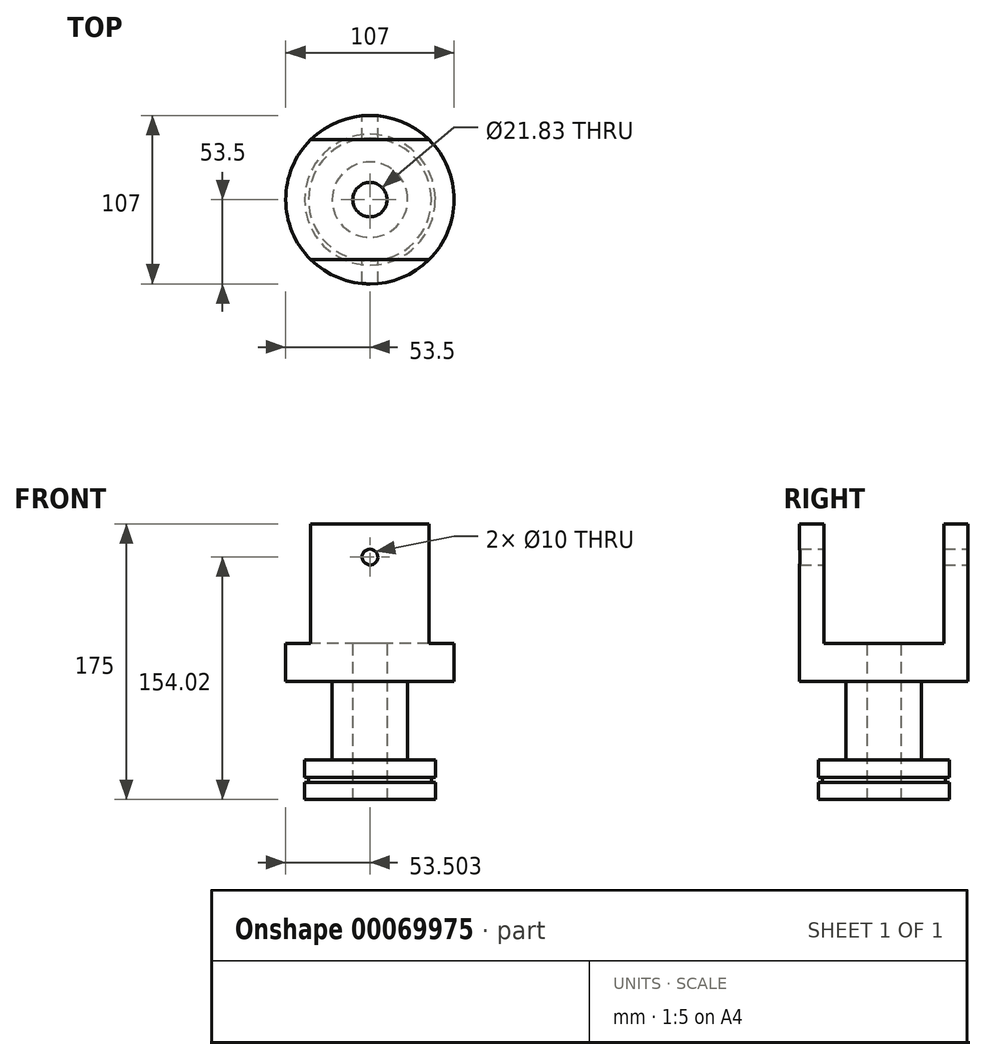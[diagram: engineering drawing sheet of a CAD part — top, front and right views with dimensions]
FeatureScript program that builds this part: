
annotation { "Feature Type Name" : "Feature", "Feature Type Description" : "" }
export const myFeature = defineFeature(function(context is Context, id is Id, definition is map)
    precondition{}
    {
        {
            var Q0;
            Q0=qCreatedBy(makeId("Top.planeOp"),FACE);
            var sketch = newSketch(context, id + "F0", { "sketchPlane" : qUnion([Q0])});
            skCircle(sketch, "E0", {"center": v(0, 0) * mm, "radius": 53.5 * mm});
            skCircle(sketch, "E1", {"center": v(0, 0) * mm, "radius": 10.91 * mm});
            skSolve(sketch);
        }
        {
            var Q0;
            Q0=makeQuery(id+"F0.imprint","IMPRINT",FACE,{"disambiguationData":[TD([[makeQuery(id+"F0.imprint","IMPRINT",EDGE,{"derivedFrom":sQuery(id+"F0.wireOp",EDGE,"E0")}),1.0]])]});
            var Q1;
            Q1=makeQuery(id+"F0.imprint","IMPRINT",FACE,{"disambiguationData":[TD([[makeQuery(id+"F0.imprint","IMPRINT",EDGE,{"derivedFrom":sQuery(id+"F0.wireOp",EDGE,"bf1bf4bc-554c-4a6b-8778-0bc88469c6b6")}),1.0]])]});
            extrude(context, id + "F1", {"entities" : qUnion([Q0, Q1]), "depth" : 100 * mm});
        }
        {
            var Q0;
            Q0=makeQuery(id+"F1.opExtrude","CAP_FACE",FACE,{"disambiguationData":[OSD([sQuery(id+"F0.wireOp",EDGE,"E0"),sQuery(id+"F0.wireOp",EDGE,"E1")])],"isStart":false});
            var sketch = newSketch(context, id + "F2", { "sketchPlane" : qUnion([Q0])});
            skLineSegment(sketch, "E2.rect.bottom", {"start": v(55, 38) * mm, "end": v(-55, 38) * mm});
            skLineSegment(sketch, "E2.rect.top", {"start": v(55, -38) * mm, "end": v(-55, -38) * mm});
            skLineSegment(sketch, "E2.rect.left", {"start": v(55, 38) * mm, "end": v(55, -38) * mm});
            skLineSegment(sketch, "E2.rect.right", {"start": v(-55, 38) * mm, "end": v(-55, -38) * mm});
            skPoint(sketch, "E2.rect.middle", {"position": v(0, 0) * mm});
            skSolve(sketch);
        }
        {
            var Q0;
            {var subQ0=sQuery(id+"F2.wireOp",EDGE,"E2.rect.bottom");var subQ1=sQuery(id+"F0.wireOp",EDGE,"E0");var subQ2=makeQuery(id+"F4ZIxcGQ2LGaYbq_1.opShell","OFFSET_EDGE",EDGE,{"disambiguationData":[OSD([subQ1]),TDD([makeQuery(id+"F1.opExtrude","CAP_EDGE",EDGE,{"disambiguationData":[OSD([subQ1])],"isStart":false})])]});var subQ3=makeQuery(id+"F2.imprint","INTERSECT",VERTEX,{"disambiguationData":[OD(0.0)],"derivedFrom":[subQ2,subQ0]});Q0=makeQuery(id+"F2.imprint","IMPRINT",FACE,{"disambiguationData":[TD([[makeQuery(id+"F2.imprint","IMPRINT",EDGE,{"disambiguationData":[TD([[subQ3,-1.0]])],"derivedFrom":subQ0}),1.0]])]});}
            var Q1;
            {var subQ0=sQuery(id+"F2.wireOp",EDGE,"E2.rect.bottom");var subQ1=sQuery(id+"F0.wireOp",EDGE,"E0");var subQ2=makeQuery(id+"F1.opExtrude","CAP_EDGE",EDGE,{"disambiguationData":[OSD([subQ1])],"isStart":false});var subQ3=makeQuery(id+"F2.imprint","INTERSECT",VERTEX,{"disambiguationData":[OD(0.0)],"derivedFrom":[subQ2,subQ0]});Q1=makeQuery(id+"F2.imprint","IMPRINT",FACE,{"disambiguationData":[TD([[makeQuery(id+"F2.imprint","IMPRINT",EDGE,{"disambiguationData":[TD([[subQ3,1.0]])],"derivedFrom":subQ2}),1.0]])]});}
            var Q2;
            {var subQ0=sQuery(id+"F2.wireOp",EDGE,"E2.rect.bottom");var subQ1=sQuery(id+"F0.wireOp",EDGE,"E0");var subQ2=makeQuery(id+"F1.opExtrude","CAP_EDGE",EDGE,{"disambiguationData":[OSD([subQ1])],"isStart":false});var subQ3=makeQuery(id+"F2.imprint","INTERSECT",VERTEX,{"disambiguationData":[OD(1.0)],"derivedFrom":[subQ2,subQ0]});Q2=makeQuery(id+"F2.imprint","IMPRINT",FACE,{"disambiguationData":[TD([[makeQuery(id+"F2.imprint","IMPRINT",EDGE,{"disambiguationData":[TD([[subQ3,-1.0]])],"derivedFrom":subQ2}),1.0]])]});}
            extrude(context, id + "F3", {"entities" : qUnion([Q0, Q1, Q2]), "oppositeDirection" : true, "depth" : 76 * mm});
        }
        {
            var Q0;
            Q0=makeQuery(id+"F3.opExtrude","SWEPT_BODY",BODY,{"disambiguationData":[OSD([sQuery(id+"F0.wireOp",EDGE,"E0"),sQuery(id+"F2.wireOp",EDGE,"E2.rect.bottom"),sQuery(id+"F2.wireOp",EDGE,"E2.rect.top")])]});
            var Q1;
            Q1=makeQuery(id+"F1.opExtrude","SWEPT_BODY",BODY,{"disambiguationData":[OSD([sQuery(id+"F0.wireOp",EDGE,"E0"),sQuery(id+"F0.wireOp",EDGE,"E1")])]});
            booleanBodies(context, id + "F4", {"operationType" : BooleanOperationType.SUBTRACTION, "tools" : qUnion([Q0]), "targets" : qUnion([Q1])});
        }
        {
            var Q0;
            Q0=makeQuery(id+"F1.opExtrude","CAP_FACE",FACE,{"disambiguationData":[OSD([sQuery(id+"F0.wireOp",EDGE,"E0"),sQuery(id+"F0.wireOp",EDGE,"E1")])],"isStart":true});
            var sketch = newSketch(context, id + "F5", { "sketchPlane" : qUnion([Q0])});
            skCircle(sketch, "E3", {"center": v(0, 0) * mm, "radius": 23.98 * mm});
            skSolve(sketch);
        }
        {
            var Q0;
            Q0=makeQuery(id+"F5.imprint","IMPRINT",FACE,{"disambiguationData":[TD([[makeQuery(id+"F5.imprint","IMPRINT",EDGE,{"derivedFrom":sQuery(id+"F5.wireOp",EDGE,"E3")}),1.0]])]});
            extrude(context, id + "F6", {"entities" : qUnion([Q0]), "operationType" : NewBodyOperationType.ADD, "depth" : 50 * mm});
        }
        {
            var Q0;
            Q0=makeQuery(id+"F6.opExtrude","CAP_FACE",FACE,{"disambiguationData":[OSD([sQuery(id+"F0.wireOp",EDGE,"E1"),sQuery(id+"F5.wireOp",EDGE,"E3")])],"isStart":false});
            var sketch = newSketch(context, id + "F7", { "sketchPlane" : qUnion([Q0])});
            skCircle(sketch, "E4", {"center": v(0, 0) * mm, "radius": 41.5 * mm});
            skSolve(sketch);
        }
        {
            var Q0;
            Q0=makeQuery(id+"F7.imprint","IMPRINT",FACE,{"disambiguationData":[TD([[makeQuery(id+"F7.imprint","IMPRINT",EDGE,{"derivedFrom":sQuery(id+"F7.wireOp",EDGE,"E4")}),1.0]])]});
            var Q1;
            Q1=makeQuery(id+"F7.imprint","IMPRINT",FACE,{"disambiguationData":[TD([[makeQuery(id+"F7.imprint","IMPRINT",EDGE,{"derivedFrom":makeQuery(id+"F6.opExtrude","CAP_EDGE",EDGE,{"disambiguationData":[OSD([sQuery(id+"F5.wireOp",EDGE,"E3")])],"isStart":false})}),1.0]])]});
            var Q2;
            Q2=makeQuery(id+"F7.imprint","IMPRINT",FACE,{"disambiguationData":[TD([[makeQuery(id+"F7.imprint","IMPRINT",EDGE,{"derivedFrom":sQuery(id+"F7.wireOp",EDGE,"RqWgMiOb-6XJQ-Qi2r-uu84-sDUD3OZ9NjxL")}),1.0]])]});
            extrude(context, id + "F8", {"entities" : qUnion([Q0, Q1, Q2]), "operationType" : NewBodyOperationType.ADD, "depth" : 11 * mm});
        }
        {
            var Q0;
            Q0=makeQuery(id+"F8.opExtrude","CAP_FACE",FACE,{"disambiguationData":[OSD([sQuery(id+"F0.wireOp",EDGE,"E1"),sQuery(id+"F7.wireOp",EDGE,"E4")])],"isStart":false});
            var sketch = newSketch(context, id + "F9", { "sketchPlane" : qUnion([Q0])});
            skCircle(sketch, "E5", {"center": v(0, 0) * mm, "radius": 39 * mm});
            skSolve(sketch);
        }
        {
            var Q0;
            Q0=makeQuery(id+"F9.imprint","IMPRINT",FACE,{"disambiguationData":[TD([[makeQuery(id+"F9.imprint","IMPRINT",EDGE,{"derivedFrom":sQuery(id+"F9.wireOp",EDGE,"E5")}),1.0]])]});
            extrude(context, id + "F10", {"entities" : qUnion([Q0]), "operationType" : NewBodyOperationType.ADD, "depth" : 3 * mm});
        }
        {
            var Q0;
            Q0=makeQuery(id+"F10.opExtrude","CAP_FACE",FACE,{"disambiguationData":[OSD([sQuery(id+"F0.wireOp",EDGE,"E1"),sQuery(id+"F9.wireOp",EDGE,"E5")])],"isStart":false});
            var sketch = newSketch(context, id + "F11", { "sketchPlane" : qUnion([Q0])});
            skCircle(sketch, "E6", {"center": v(0, 0) * mm, "radius": 41.5 * mm});
            skSolve(sketch);
        }
        {
            var Q0;
            Q0=makeQuery(id+"F11.imprint","IMPRINT",FACE,{"disambiguationData":[TD([[makeQuery(id+"F11.imprint","IMPRINT",EDGE,{"derivedFrom":sQuery(id+"F11.wireOp",EDGE,"E6")}),1.0]])]});
            var Q1;
            Q1=makeQuery(id+"F11.imprint","IMPRINT",FACE,{"disambiguationData":[TD([[makeQuery(id+"F11.imprint","IMPRINT",EDGE,{"derivedFrom":makeQuery(id+"F10.opExtrude","CAP_EDGE",EDGE,{"disambiguationData":[OSD([sQuery(id+"F9.wireOp",EDGE,"E5")])],"isStart":false})}),1.0]])]});
            extrude(context, id + "F12", {"entities" : qUnion([Q0, Q1]), "operationType" : NewBodyOperationType.ADD, "depth" : 11 * mm});
        }
        {
            var Q0;
            Q0=qCreatedBy(makeId("Front.planeOp"),FACE);
            var sketch = newSketch(context, id + "F13", { "sketchPlane" : qUnion([Q0])});
            skCircle(sketch, "E7", {"center": v(-63.12, -22.98) * mm, "radius": 5 * mm});
            skSolve(sketch);
        }
        {
            var Q0;
            Q0=makeQuery(id+"F13.imprint","IMPRINT",FACE,{"disambiguationData":[TD([[makeQuery(id+"F13.imprint","IMPRINT",EDGE,{"derivedFrom":sQuery(id+"F13.wireOp",EDGE,"E7")}),1.0]])]});
            extrude(context, id + "F14", {"entities" : qUnion([Q0]), "depth" : 125 * mm});
        }
        {
            var Q0;
            Q0=makeQuery(id+"F14.opExtrude","SWEPT_BODY",BODY,{"disambiguationData":[OSD([sQuery(id+"F13.wireOp",EDGE,"E7")])]});
            transform(context, id + "F15", {"entities" : qUnion([Q0]), "transformType" : TransformType.TRANSLATION_3D, "dx" : 63.12 * mm, "dy" : 62.74 * mm, "dz" : 102 * mm, "makeCopy" : false});
        }
        {
            var Q0;
            Q0=makeQuery(id+"F14.opExtrude","SWEPT_BODY",BODY,{"disambiguationData":[OSD([sQuery(id+"F13.wireOp",EDGE,"E7")])]});
            var Q1;
            Q1=makeQuery(id+"F1.opExtrude","SWEPT_BODY",BODY,{"disambiguationData":[OSD([sQuery(id+"F0.wireOp",EDGE,"E0"),sQuery(id+"F0.wireOp",EDGE,"E1")])]});
            booleanBodies(context, id + "F16", {"operationType" : BooleanOperationType.SUBTRACTION, "tools" : qUnion([Q0]), "targets" : qUnion([Q1])});
        }
    });
